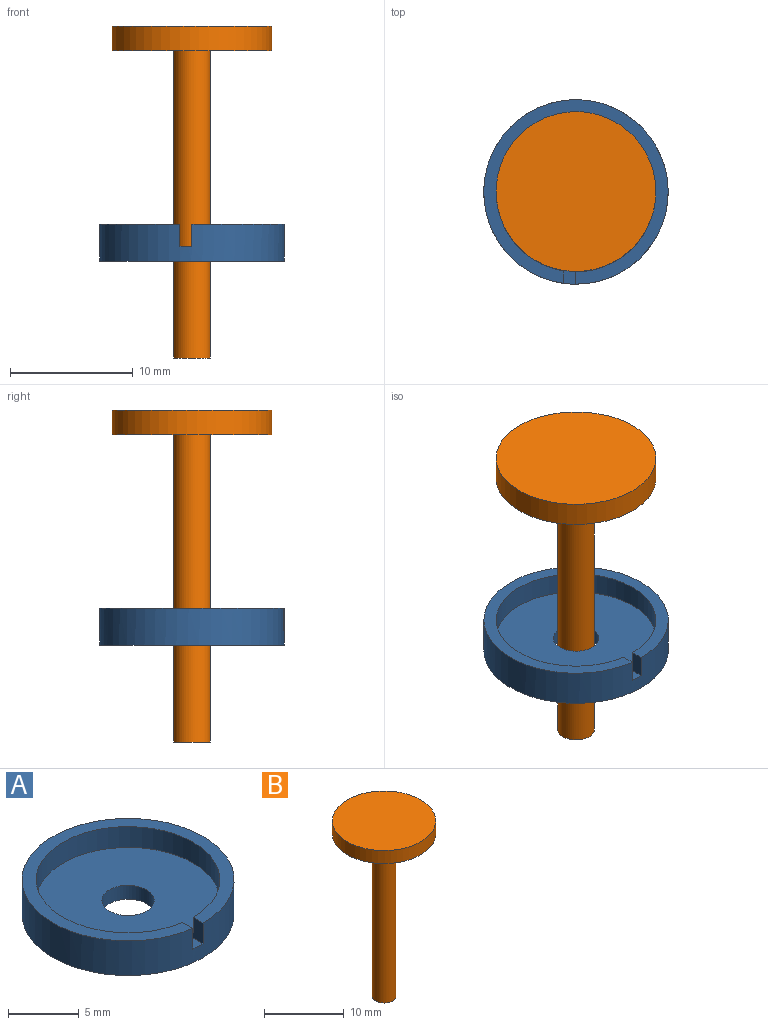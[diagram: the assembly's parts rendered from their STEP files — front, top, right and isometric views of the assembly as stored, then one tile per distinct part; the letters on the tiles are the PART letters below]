
ASSEMBLY  parts=2 mates=1
PART A: 8 faces, bbox 15x15x3 mm
  f0: cylinder r=7.5mm len=15mm, axis (0,0,-1), area 139.6mm2, adj f1,f2,f4,f5,f6
  f1: plane 15x15mm, normal (0,0,1), area 43mm2, adj f0,f3,f5,f6
  f2: plane 15x15mm, normal (0,0,-1), area 166mm2, adj f0,f7
  f3: cylinder r=6.5mm len=13mm, axis (0,0,1), area 71.8mm2, adj f1,f4,f5,f6
  f4: plane 14x13mm, normal (0,0,1), area 123mm2, adj f0,f3,f5,f6,f7
  f5: plane 1.8x1.01mm, normal (1,0,0), area 1.8mm2, adj f0,f1,f3,f4
  f6: plane 1.8x1mm, normal (-1,0,0), area 1.8mm2, adj f0,f1,f3,f4
  f7: cylinder r=1.85mm len=3.7mm, axis (0,0,1), area 13.9mm2, adj f2,f4
PART B: 5 faces, bbox 13x13x27 mm
  f0: cylinder r=6.5mm len=13mm, axis (0,0,-1), area 81.7mm2, adj f1,f2
  f1: plane 13x13mm, normal (0,0,1), area 132.7mm2, adj f0
  f2: plane 13x13mm, normal (0,0,-1), area 125.7mm2, adj f0,f3
  f3: cylinder r=1.5mm len=25mm, axis (0,0,-1), area 235.6mm2, adj f2,f4
  f4: plane 3x3mm, normal (0,0,-1), area 7.1mm2, adj f3
PLACE A t=(-1.2,-0.5,-1.2)mm fixed
PLACE B t=(-1.2,-0.5,-9.08)mm
MATE slider B.f0 <-> A.f0  axis (0,0,-1) through (-1.2,-0.5,3.42)mm
